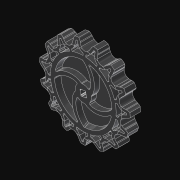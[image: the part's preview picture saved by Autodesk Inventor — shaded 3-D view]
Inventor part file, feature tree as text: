
AUTODESK INVENTOR PART (.ipt)
format: ipt  version: 2021.3 (Build 253353010, 353A)  size: 4,182,016 bytes
history: native  units: in
note: dims shown in document units (in); Inventor stores cm internally (conversion verified against a paired STEP export)
features: plane x2, extrude x2, sketch x2, other x1, imported_body x1
ambient origin geometry x8: Origin, YZ Plane, XZ Plane, XY Plane, X Axis, Y Axis, Z Axis, Center Point
bodies: Body1 (feature_tree)
feature tree (8):
  parser-record x1  (decoder bookkeeping rows leaked as tree rows — omitted from the tree; the rows remain in map.json)
  imported_body  "Base1"
  plane  "Work Plane1"
  extrude  "Extrusion1"  Depth=1.0in TaperAngle=0.0deg
  plane  "Work Plane2"
  extrude  "Extrusion2"  Depth=1.0in TaperAngle=0.0deg
  sketch  "Sketch1"  dims[d2=2.0in d3=1.0in d4=0.0in]
  sketch  "Sketch2"  dims[d5=-3.0in d6=1.0in d7=0.0in]
